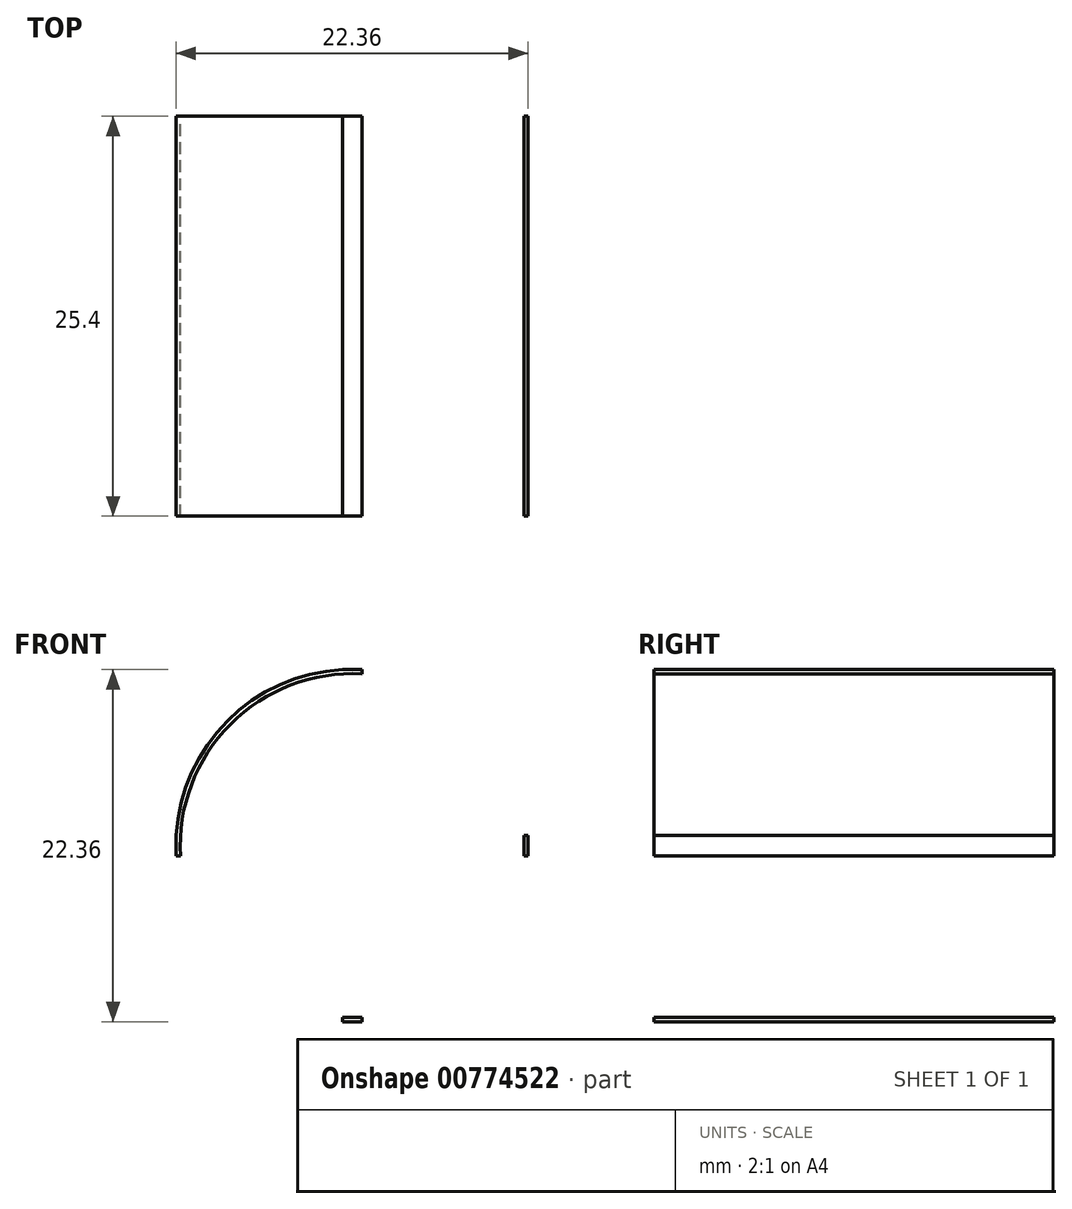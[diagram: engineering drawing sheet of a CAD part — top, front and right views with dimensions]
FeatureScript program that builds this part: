
annotation { "Feature Type Name" : "Feature", "Feature Type Description" : "" }
export const myFeature = defineFeature(function(context is Context, id is Id, definition is map)
    precondition{}
    {
        {
            var Q0;
            Q0=qCreatedBy(makeId("Front.planeOp"),FACE);
            var sketch = newSketch(context, id + "F0", { "sketchPlane" : qUnion([Q0])});
            skCircle(sketch, "E0", {"center": v(0, 0) * mm, "radius": 11.2 * mm});
            skCircle(sketch, "E1", {"center": v(0, 0) * mm, "radius": 10.92 * mm});
            skCircle(sketch, "E2", {"center": v(0, 0) * mm, "radius": 10.67 * mm});
            skCircle(sketch, "E3", {"center": v(0, 0) * mm, "radius": 10.41 * mm});
            skCircle(sketch, "E4", {"center": v(0, 0) * mm, "radius": 10.16 * mm});
            skCircle(sketch, "E5", {"center": v(0, 0) * mm, "radius": 9.9 * mm});
            skCircle(sketch, "E6", {"center": v(0, 0) * mm, "radius": 9.65 * mm});
            skCircle(sketch, "E7", {"center": v(0, 0) * mm, "radius": 9.4 * mm});
            skCircle(sketch, "E8", {"center": v(0, 0) * mm, "radius": 9.14 * mm});
            skCircle(sketch, "E9", {"center": v(0, 0) * mm, "radius": 8.9 * mm});
            skCircle(sketch, "E10", {"center": v(0, 0) * mm, "radius": 8.64 * mm});
            skCircle(sketch, "E11", {"center": v(0, 0) * mm, "radius": 8.38 * mm});
            skCircle(sketch, "E12", {"center": v(0, 0) * mm, "radius": 8.13 * mm});
            skCircle(sketch, "E13", {"center": v(0, 0) * mm, "radius": 7.87 * mm});
            skCircle(sketch, "E14", {"center": v(0, 0) * mm, "radius": 7.62 * mm});
            skCircle(sketch, "E15", {"center": v(0, 0) * mm, "radius": 7.37 * mm});
            skCircle(sketch, "E16", {"center": v(0, 0) * mm, "radius": 6.86 * mm});
            skCircle(sketch, "E17", {"center": v(0, 0) * mm, "radius": 7.11 * mm});
            skCircle(sketch, "E18", {"center": v(0, 0) * mm, "radius": 6.6 * mm});
            skCircle(sketch, "E19", {"center": v(0, 0) * mm, "radius": 6.35 * mm});
            skCircle(sketch, "E20", {"center": v(0, 0) * mm, "radius": 6.1 * mm});
            skCircle(sketch, "E21", {"center": v(0, 0) * mm, "radius": 5.84 * mm});
            skCircle(sketch, "E22", {"center": v(0, 0) * mm, "radius": 5.59 * mm});
            skCircle(sketch, "E23", {"center": v(0, 0) * mm, "radius": 5.33 * mm});
            skCircle(sketch, "E24", {"center": v(0, 0) * mm, "radius": 5.08 * mm});
            skCircle(sketch, "E25", {"center": v(0, 0) * mm, "radius": 4.83 * mm});
            skCircle(sketch, "E26", {"center": v(0, 0) * mm, "radius": 4.32 * mm});
            skCircle(sketch, "E27", {"center": v(0, 0) * mm, "radius": 4.57 * mm});
            skCircle(sketch, "E28", {"center": v(0, 0) * mm, "radius": 4.06 * mm});
            skCircle(sketch, "E29", {"center": v(0, 0) * mm, "radius": 3.81 * mm});
            skCircle(sketch, "E30", {"center": v(0, 0) * mm, "radius": 3.56 * mm});
            skCircle(sketch, "E31", {"center": v(0, 0) * mm, "radius": 3.3 * mm});
            skCircle(sketch, "E32", {"center": v(0, 0) * mm, "radius": 2.8 * mm});
            skCircle(sketch, "E33", {"center": v(0, 0) * mm, "radius": 3.05 * mm});
            skCircle(sketch, "E34", {"center": v(0, 0) * mm, "radius": 2.54 * mm});
            skCircle(sketch, "E35", {"center": v(0, 0) * mm, "radius": 2.29 * mm});
            skCircle(sketch, "E36", {"center": v(0, 0) * mm, "radius": 2.03 * mm});
            skCircle(sketch, "E37", {"center": v(0, 0) * mm, "radius": 1.78 * mm});
            skCircle(sketch, "E38", {"center": v(0, 0) * mm, "radius": 1.52 * mm});
            skLineSegment(sketch, "E39.bottom", {"start": v(-11.18, -0.65) * mm, "end": v(11.18, -0.65) * mm});
            skLineSegment(sketch, "E39.top", {"start": v(-11.18, 0.65) * mm, "end": v(11.18, 0.65) * mm});
            skLineSegment(sketch, "E39.left", {"start": v(-11.18, -0.65) * mm, "end": v(-11.18, 0.65) * mm});
            skLineSegment(sketch, "E39.right", {"start": v(11.18, -0.65) * mm, "end": v(11.18, 0.65) * mm});
            skLineSegment(sketch, "E40.bottom", {"start": v(0, 0.65) * mm, "end": v(0, 0.65) * mm});
            skLineSegment(sketch, "E40.top", {"start": v(0, -0.65) * mm, "end": v(0, -0.65) * mm});
            skLineSegment(sketch, "E40.left", {"start": v(0, 0.65) * mm, "end": v(0, -0.65) * mm});
            skLineSegment(sketch, "E40.right", {"start": v(0, 0.65) * mm, "end": v(0, -0.65) * mm});
            skLineSegment(sketch, "E41.bottom", {"start": v(0.62, -11.18) * mm, "end": v(-0.62, -11.18) * mm});
            skLineSegment(sketch, "E41.top", {"start": v(0.62, 11.18) * mm, "end": v(-0.62, 11.18) * mm});
            skLineSegment(sketch, "E41.left", {"start": v(0.62, -11.18) * mm, "end": v(0.62, 11.18) * mm});
            skLineSegment(sketch, "E41.right", {"start": v(-0.62, -11.18) * mm, "end": v(-0.62, 11.18) * mm});
            skSolve(sketch);
        }
        {
            var Q0;
            {var subQ0=sQuery(id+"F0.wireOp",EDGE,"E39.bottom");var subQ5=sQuery(id+"F0.wireOp",EDGE,"E1");var subQ6=makeQuery(id+"F0.imprint","INTERSECT",VERTEX,{"disambiguationData":[OD(0.0)],"derivedFrom":[subQ5,subQ0]});Q0=makeQuery(id+"F0.imprint","IMPRINT",FACE,{"disambiguationData":[TD([[makeQuery(id+"F0.imprint","IMPRINT",EDGE,{"disambiguationData":[TD([[subQ6,-1.0]])],"derivedFrom":subQ5}),-1.0]])]});}
            var Q1;
            {var subQ5=sQuery(id+"F0.wireOp",EDGE,"E39.left");Q1=makeQuery(id+"F0.imprint","IMPRINT",FACE,{"disambiguationData":[TD([[makeQuery(id+"F0.imprint","IMPRINT",EDGE,{"derivedFrom":subQ5}),-1.0]])]});}
            var Q2;
            {var subQ3=sQuery(id+"F0.wireOp",EDGE,"E41.right");var subQ5=sQuery(id+"F0.wireOp",EDGE,"E1");var subQ7=makeQuery(id+"F0.imprint","INTERSECT",VERTEX,{"disambiguationData":[OD(0.0)],"derivedFrom":[subQ5,subQ3]});Q2=makeQuery(id+"F0.imprint","IMPRINT",FACE,{"disambiguationData":[TD([[makeQuery(id+"F0.imprint","IMPRINT",EDGE,{"disambiguationData":[TD([[subQ7,-1.0]])],"derivedFrom":subQ5}),-1.0]])]});}
            var Q3;
            {var subQ5=sQuery(id+"F0.wireOp",EDGE,"E41.top");Q3=makeQuery(id+"F0.imprint","IMPRINT",FACE,{"disambiguationData":[TD([[makeQuery(id+"F0.imprint","IMPRINT",EDGE,{"derivedFrom":subQ5}),1.0]])]});}
            var Q4;
            {var subQ3=sQuery(id+"F0.wireOp",EDGE,"E41.left");var subQ5=sQuery(id+"F0.wireOp",EDGE,"E1");var subQ6=makeQuery(id+"F0.imprint","INTERSECT",VERTEX,{"disambiguationData":[OD(0.0)],"derivedFrom":[subQ5,subQ3]});Q4=makeQuery(id+"F0.imprint","IMPRINT",FACE,{"disambiguationData":[TD([[makeQuery(id+"F0.imprint","IMPRINT",EDGE,{"disambiguationData":[TD([[subQ6,1.0]])],"derivedFrom":subQ5}),-1.0]])]});}
            var Q5;
            {var subQ5=sQuery(id+"F0.wireOp",EDGE,"E39.right");Q5=makeQuery(id+"F0.imprint","IMPRINT",FACE,{"disambiguationData":[TD([[makeQuery(id+"F0.imprint","IMPRINT",EDGE,{"derivedFrom":subQ5}),1.0]])]});}
            var Q6;
            {var subQ3=sQuery(id+"F0.wireOp",EDGE,"E41.left");var subQ5=sQuery(id+"F0.wireOp",EDGE,"E1");var subQ7=makeQuery(id+"F0.imprint","INTERSECT",VERTEX,{"disambiguationData":[OD(1.0)],"derivedFrom":[subQ5,subQ3]});Q6=makeQuery(id+"F0.imprint","IMPRINT",FACE,{"disambiguationData":[TD([[makeQuery(id+"F0.imprint","IMPRINT",EDGE,{"disambiguationData":[TD([[subQ7,-1.0]])],"derivedFrom":subQ5}),-1.0]])]});}
            var Q7;
            {var subQ5=sQuery(id+"F0.wireOp",EDGE,"E41.bottom");Q7=makeQuery(id+"F0.imprint","IMPRINT",FACE,{"disambiguationData":[TD([[makeQuery(id+"F0.imprint","IMPRINT",EDGE,{"derivedFrom":subQ5}),-1.0]])]});}
            extrude(context, id + "F1", {"entities" : qUnion([Q0, Q1, Q2, Q3, Q4, Q5, Q6, Q7]), "depth" : 25.4 * mm, "offsetDistance" : 25.4 * mm});
        }
        {
            var Q0;
            Q0=sQuery(id+"F0.wireOp",EDGE,"E1");
            extrude(context, id + "F2", {"bodyType" : ToolBodyType.SURFACE, "surfaceEntities" : qUnion([Q0]), "depth" : 25.4 * mm, "offsetDistance" : 25.4 * mm});
        }
    });
